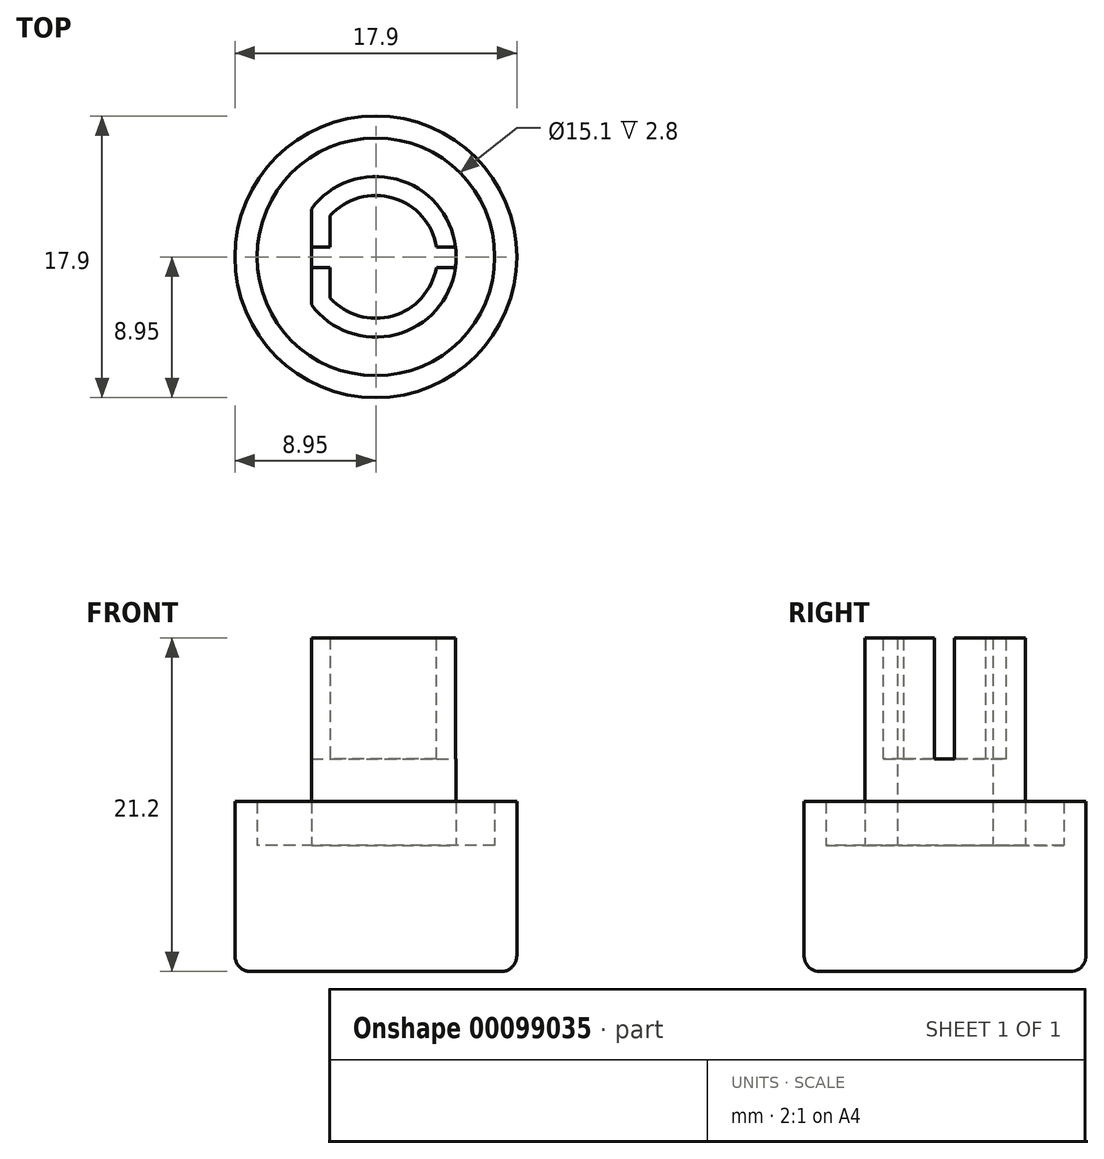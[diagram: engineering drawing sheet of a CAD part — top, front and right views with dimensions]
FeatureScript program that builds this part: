
annotation { "Feature Type Name" : "Feature", "Feature Type Description" : "" }
export const myFeature = defineFeature(function(context is Context, id is Id, definition is map)
    precondition{}
    {
        {
            var Q0;
            Q0=qCreatedBy(makeId("Top.planeOp"),FACE);
            var sketch = newSketch(context, id + "F0", { "sketchPlane" : qUnion([Q0])});
            skCircle(sketch, "E0", {"center": v(0, 0) * mm, "radius": 8.95 * mm});
            skSolve(sketch);
        }
        {
            var Q0;
            Q0=makeQuery(id+"F0.imprint","IMPRINT",FACE,{"disambiguationData":[TD([[makeQuery(id+"F0.imprint","IMPRINT",EDGE,{"derivedFrom":sQuery(id+"F0.wireOp",EDGE,"E0")}),1.0]])]});
            extrude(context, id + "F1", {"entities" : qUnion([Q0]), "depth" : 8 * mm});
        }
        {
            var Q0;
            Q0=makeQuery(id+"F1.opExtrude","CAP_FACE",FACE,{"disambiguationData":[OSD([sQuery(id+"F0.wireOp",EDGE,"E0")])],"isStart":false});
            var sketch = newSketch(context, id + "F2", { "sketchPlane" : qUnion([Q0])});
            skCircle(sketch, "E1", {"center": v(0, 0) * mm, "radius": 7.55 * mm});
            skSolve(sketch);
        }
        {
            var Q0;
            Q0=makeQuery(id+"F2.imprint","IMPRINT",FACE,{"disambiguationData":[TD([[makeQuery(id+"F2.imprint","IMPRINT",EDGE,{"derivedFrom":sQuery(id+"F2.wireOp",EDGE,"E1")}),-1.0]])]});
            extrude(context, id + "F3", {"entities" : qUnion([Q0]), "operationType" : NewBodyOperationType.ADD, "depth" : 2.8 * mm});
        }
        {
            var Q0;
            Q0=makeQuery(id+"F1.opExtrude","CAP_FACE",FACE,{"disambiguationData":[OSD([sQuery(id+"F0.wireOp",EDGE,"E0")])],"isStart":false});
            var sketch = newSketch(context, id + "F4", { "sketchPlane" : qUnion([Q0])});
            skCircle(sketch, "E2", {"center": v(0, 0) * mm, "radius": 5.1 * mm});
            skLineSegment(sketch, "E3", {"start": v(-4.1, 5.65) * mm, "end": v(-4.1, -5.57) * mm});
            skSolve(sketch);
        }
        {
            var Q0;
            {var subQ0=sQuery(id+"F4.wireOp",EDGE,"E3");var subQ1=sQuery(id+"F4.wireOp",EDGE,"E2");var subQ2=makeQuery(id+"F4.imprint","INTERSECT",VERTEX,{"disambiguationData":[OD(0.0)],"derivedFrom":[subQ1,subQ0]});Q0=makeQuery(id+"F4.imprint","IMPRINT",FACE,{"disambiguationData":[TD([[makeQuery(id+"F4.imprint","IMPRINT",EDGE,{"disambiguationData":[TD([[subQ2,-1.0]])],"derivedFrom":subQ1}),1.0]])]});}
            extrude(context, id + "F5", {"entities" : qUnion([Q0]), "operationType" : NewBodyOperationType.ADD, "depth" : 13.2 * mm});
        }
        {
            var Q0;
            Q0=makeQuery(id+"F1.opExtrude","CAP_EDGE",EDGE,{"disambiguationData":[OSD([sQuery(id+"F0.wireOp",EDGE,"E0")])],"isStart":true});
            fillet(context, id + "F6", {"entities" : qUnion([Q0]), "radius" : 1 * mm, "tangentPropagation" : true, "allowEdgeOverflow" : false});
        }
        {
            var Q0;
            Q0=makeQuery(id+"F5.opExtrude","CAP_FACE",FACE,{"disambiguationData":[OSD([sQuery(id+"F4.wireOp",EDGE,"E2"),sQuery(id+"F4.wireOp",EDGE,"E3")])],"isStart":false});
            var sketch = newSketch(context, id + "F7", { "sketchPlane" : qUnion([Q0])});
            skArc(sketch, "E4", {"start": v(-2.9, -2.6) * mm, "mid": v(3.9, 0) * mm, "end": v(-2.9, 2.6) * mm});
            skLineSegment(sketch, "E5", {"start": v(-2.9, 2.6) * mm, "end": v(-2.9, -2.6) * mm});
            skSolve(sketch);
        }
        {
            var Q0;
            Q0=makeQuery(id+"F7.imprint","IMPRINT",FACE,{"disambiguationData":[TD([[makeQuery(id+"F7.imprint","IMPRINT",EDGE,{"derivedFrom":sQuery(id+"F7.wireOp",EDGE,"E4")}),1.0]])]});
            extrude(context, id + "F8", {"entities" : qUnion([Q0]), "operationType" : NewBodyOperationType.REMOVE, "oppositeDirection" : true, "depth" : 7.7 * mm});
        }
        {
            var Q0;
            Q0=makeQuery(id+"F8.boolean.opBoolean","COPY",FACE,{"derivedFrom":makeQuery(id+"F8.opExtrude","SWEPT_FACE",FACE,{"disambiguationData":[OSD([sQuery(id+"F7.wireOp",EDGE,"E5")])]})});
            var sketch = newSketch(context, id + "F9", { "sketchPlane" : qUnion([Q0])});
            skLineSegment(sketch, "E6.bottom", {"start": v(-0.68, 13.5) * mm, "end": v(0.6, 13.5) * mm});
            skLineSegment(sketch, "E6.top", {"start": v(-0.68, 21.2) * mm, "end": v(0.6, 21.2) * mm});
            skLineSegment(sketch, "E6.left", {"start": v(-0.68, 13.5) * mm, "end": v(-0.68, 21.2) * mm});
            skLineSegment(sketch, "E6.right", {"start": v(0.6, 13.5) * mm, "end": v(0.6, 21.2) * mm});
            skSolve(sketch);
        }
        {
            var Q0;
            Q0=makeQuery(id+"F9.imprint","IMPRINT",FACE,{"disambiguationData":[TD([[makeQuery(id+"F9.imprint","IMPRINT",EDGE,{"derivedFrom":sQuery(id+"F9.wireOp",EDGE,"E6.bottom")}),-1.0]])]});
            extrude(context, id + "F10", {"entities" : qUnion([Q0]), "operationType" : NewBodyOperationType.REMOVE, "oppositeDirection" : true, "depth" : 1.5 * mm, "hasSecondDirection" : true, "secondDirectionOppositeDirection" : false, "secondDirectionDepth" : 8 * mm});
        }
    });
